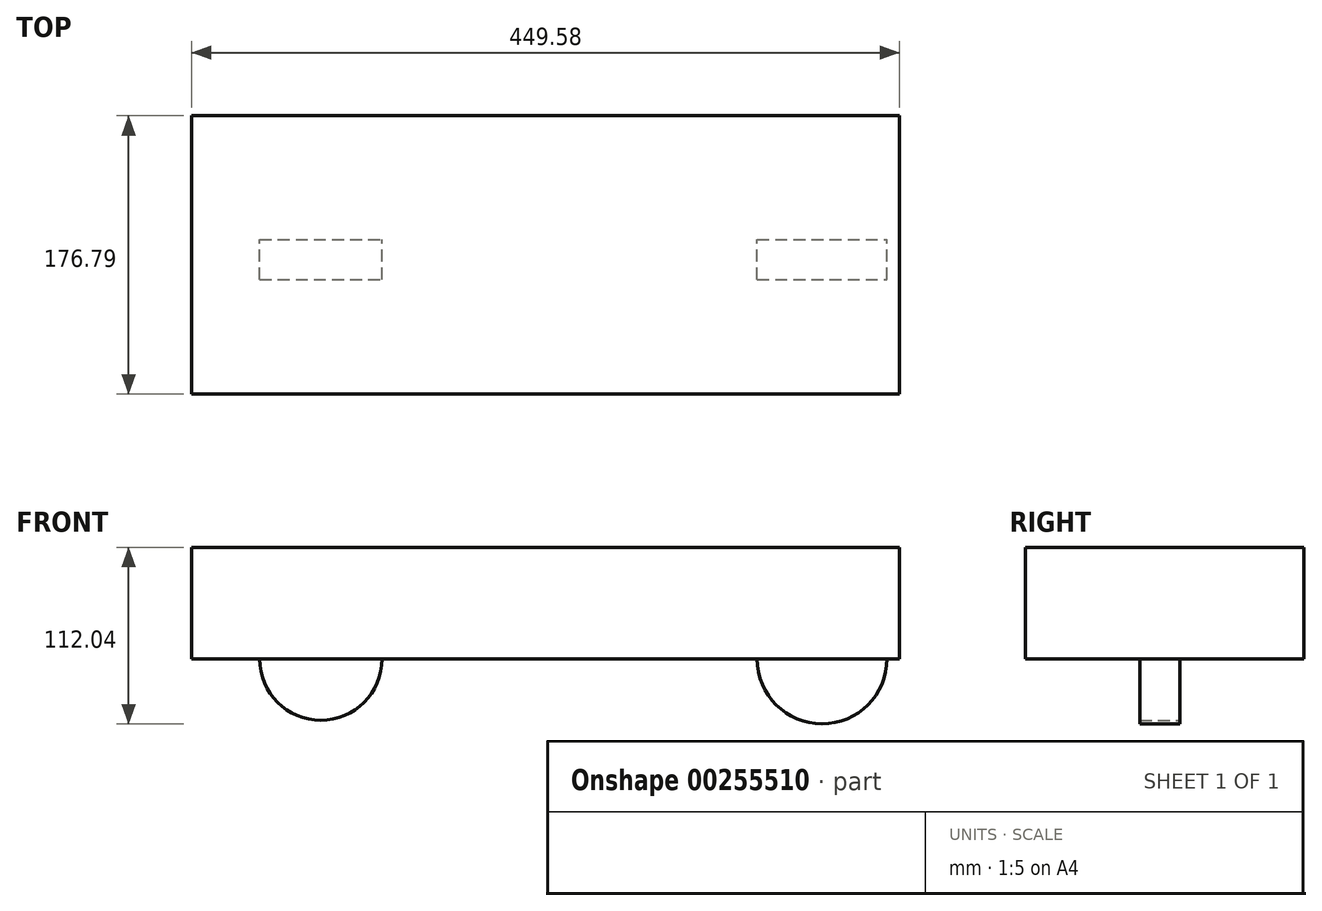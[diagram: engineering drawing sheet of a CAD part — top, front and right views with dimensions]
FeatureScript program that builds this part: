
annotation { "Feature Type Name" : "Feature", "Feature Type Description" : "" }
export const myFeature = defineFeature(function(context is Context, id is Id, definition is map)
    precondition{}
    {
        {
            var Q0;
            Q0=qCreatedBy(makeId("Top.planeOp"),FACE);
            var sketch = newSketch(context, id + "F0", { "sketchPlane" : qUnion([Q0])});
            skLineSegment(sketch, "E0.bottom", {"start": v(-225.25, 78.72) * mm, "end": v(224.33, 78.72) * mm});
            skLineSegment(sketch, "E0.top", {"start": v(-225.25, -98.07) * mm, "end": v(224.33, -98.07) * mm});
            skLineSegment(sketch, "E0.left", {"start": v(-225.25, 78.72) * mm, "end": v(-225.25, -98.07) * mm});
            skLineSegment(sketch, "E0.right", {"start": v(224.33, 78.72) * mm, "end": v(224.33, -98.07) * mm});
            skSolve(sketch);
        }
        {
            var Q0;
            Q0=makeQuery(id+"F0.imprint","IMPRINT",FACE,{"disambiguationData":[TD([[makeQuery(id+"F0.imprint","IMPRINT",EDGE,{"derivedFrom":sQuery(id+"F0.wireOp",EDGE,"E0.bottom")}),-1.0]])]});
            extrude(context, id + "F1", {"entities" : qUnion([Q0]), "depth" : 70.87 * mm});
        }
        {
            var Q0;
            Q0=qCreatedBy(makeId("Front.planeOp"),FACE);
            var sketch = newSketch(context, id + "F2", { "sketchPlane" : qUnion([Q0])});
            skCircle(sketch, "E1", {"center": v(175.14, 0) * mm, "radius": 41.17 * mm});
            skCircle(sketch, "E2", {"center": v(-143.22, 0) * mm, "radius": 38.84 * mm});
            skSolve(sketch);
        }
        {
            var Q0;
            Q0=makeQuery(id+"F2.imprint","IMPRINT",FACE,{"disambiguationData":[TD([[makeQuery(id+"F2.imprint","IMPRINT",EDGE,{"derivedFrom":sQuery(id+"F2.wireOp",EDGE,"E2")}),1.0]])]});
            var Q1;
            Q1=makeQuery(id+"F2.imprint","IMPRINT",FACE,{"disambiguationData":[TD([[makeQuery(id+"F2.imprint","IMPRINT",EDGE,{"derivedFrom":sQuery(id+"F2.wireOp",EDGE,"E1")}),1.0]])]});
            extrude(context, id + "F3", {"entities" : qUnion([Q0, Q1]), "operationType" : NewBodyOperationType.ADD, "depth" : 25.4 * mm});
        }
    });
